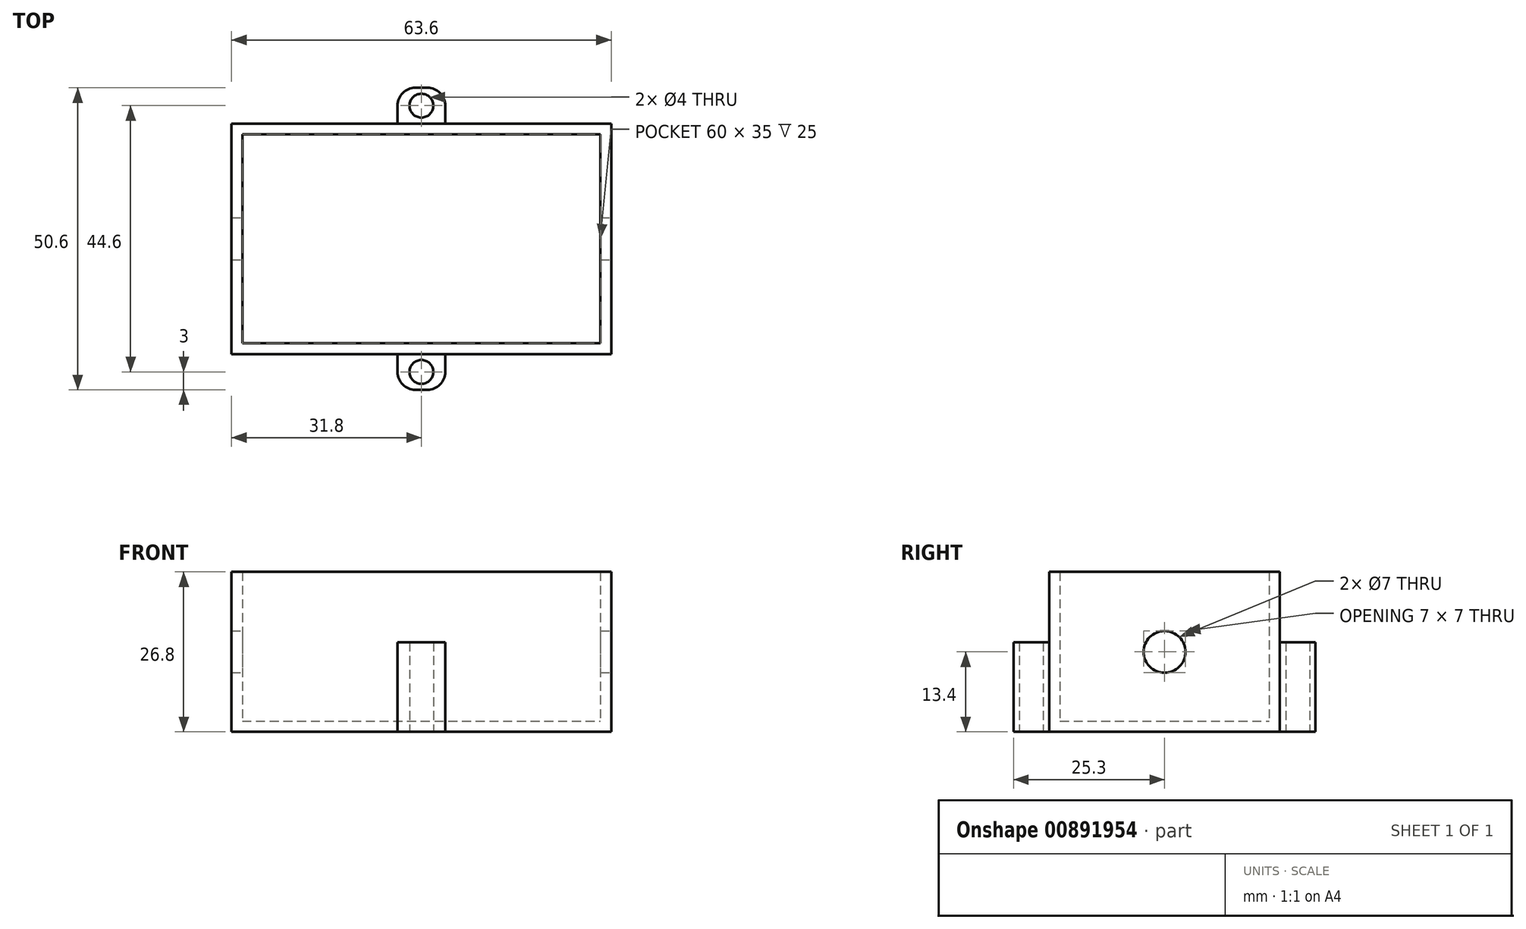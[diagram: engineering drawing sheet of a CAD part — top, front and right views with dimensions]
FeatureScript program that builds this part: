
annotation { "Feature Type Name" : "Feature", "Feature Type Description" : "" }
export const myFeature = defineFeature(function(context is Context, id is Id, definition is map)
    precondition{}
    {
        {
            var Q0;
            Q0=qCreatedBy(makeId("Top.planeOp"),FACE);
            var sketch = newSketch(context, id + "F0", { "sketchPlane" : qUnion([Q0])});
            skLineSegment(sketch, "E0.bottom", {"start": v(0, 0) * mm, "end": v(60, 0) * mm});
            skLineSegment(sketch, "E0.top", {"start": v(0, 35) * mm, "end": v(60, 35) * mm});
            skLineSegment(sketch, "E0.left", {"start": v(0, 0) * mm, "end": v(0, 35) * mm});
            skLineSegment(sketch, "E0.right", {"start": v(60, 0) * mm, "end": v(60, 35) * mm});
            skLineSegment(sketch, "E1.bottom", {"start": v(-1.8, 36.8) * mm, "end": v(61.8, 36.8) * mm});
            skLineSegment(sketch, "E1.top", {"start": v(-1.8, -1.8) * mm, "end": v(61.8, -1.8) * mm});
            skLineSegment(sketch, "E1.left", {"start": v(-1.8, 36.8) * mm, "end": v(-1.8, -1.8) * mm});
            skLineSegment(sketch, "E1.right", {"start": v(61.8, 36.8) * mm, "end": v(61.8, -1.8) * mm});
            skLineSegment(sketch, "E2", {"start": v(30, -1.8) * mm, "end": v(30, 36.8) * mm, "construction": true});
            skLineSegment(sketch, "E3", {"start": v(26, -1.8) * mm, "end": v(34, -1.8) * mm});
            skLineSegment(sketch, "E4", {"start": v(26, -1.8) * mm, "end": v(26, -4.8) * mm});
            skLineSegment(sketch, "E5", {"start": v(29, -7.8) * mm, "end": v(31, -7.8) * mm});
            skLineSegment(sketch, "E6", {"start": v(34, -4.8) * mm, "end": v(34, -1.8) * mm});
            skPoint(sketch, "E7.visualSharp", {"position": v(26, -7.8) * mm});
            skArc(sketch, "E7.filletArc", {"start": v(26, -4.8) * mm, "mid": v(26.88, -6.92) * mm, "end": v(29, -7.8) * mm});
            skPoint(sketch, "E8.visualSharp", {"position": v(34, -7.8) * mm});
            skArc(sketch, "E8.filletArc", {"start": v(31, -7.8) * mm, "mid": v(33.12, -6.92) * mm, "end": v(34, -4.8) * mm});
            skCircle(sketch, "E9", {"center": v(30, -4.8) * mm, "radius": 2 * mm});
            skLineSegment(sketch, "E10", {"start": v(0, 17.5) * mm, "end": v(60, 17.5) * mm, "construction": true});
            skLineSegment(sketch, "E11.MirrorCS", {"start": v(29, 42.8) * mm, "end": v(31, 42.8) * mm});
            skArc(sketch, "E12.MirrorCS", {"start": v(26, 39.8) * mm, "mid": v(26.88, 41.92) * mm, "end": v(29, 42.8) * mm});
            skLineSegment(sketch, "E13.MirrorCS", {"start": v(26, 36.8) * mm, "end": v(26, 39.8) * mm});
            skLineSegment(sketch, "E14.MirrorCS", {"start": v(34, 39.8) * mm, "end": v(34, 36.8) * mm});
            skArc(sketch, "E15.MirrorCS", {"start": v(31, 42.8) * mm, "mid": v(33.12, 41.92) * mm, "end": v(34, 39.8) * mm});
            skCircle(sketch, "E16.MirrorC", {"center": v(30, 39.8) * mm, "radius": 2 * mm});
            skSolve(sketch);
        }
        {
            var Q0;
            Q0=makeQuery(id+"F0.imprint","IMPRINT",FACE,{"disambiguationData":[TD([[makeQuery(id+"F0.imprint","IMPRINT",EDGE,{"derivedFrom":sQuery(id+"F0.wireOp",EDGE,"E0.bottom")}),-1.0]])]});
            var Q1;
            Q1=makeQuery(id+"F0.imprint","IMPRINT",FACE,{"disambiguationData":[TD([[makeQuery(id+"F0.imprint","IMPRINT",EDGE,{"derivedFrom":sQuery(id+"F0.wireOp",EDGE,"E0.bottom")}),1.0]])]});
            extrude(context, id + "F1", {"entities" : qUnion([Q0, Q1]), "depth" : 1.8 * mm, "offsetDistance" : 25 * mm});
        }
        {
            var Q0;
            Q0=makeQuery(id+"F1.opExtrude","CAP_FACE",FACE,{"disambiguationData":[OSD([sQuery(id+"F0.wireOp",EDGE,"E1.bottom"),sQuery(id+"F0.wireOp",EDGE,"E1.top"),sQuery(id+"F0.wireOp",EDGE,"E1.left"),sQuery(id+"F0.wireOp",EDGE,"E1.right")])],"isStart":false});
            var sketch = newSketch(context, id + "F2", { "sketchPlane" : qUnion([Q0])});
            skLineSegment(sketch, "E17.0", {"start": v(0, 0) * mm, "end": v(60, 0) * mm});
            skLineSegment(sketch, "E17.1", {"start": v(0, 35) * mm, "end": v(60, 35) * mm});
            skLineSegment(sketch, "E17.2", {"start": v(0, 0) * mm, "end": v(0, 35) * mm});
            skLineSegment(sketch, "E17.3", {"start": v(60, 0) * mm, "end": v(60, 35) * mm});
            skLineSegment(sketch, "E17.4", {"start": v(-1.8, 36.8) * mm, "end": v(61.8, 36.8) * mm});
            skLineSegment(sketch, "E17.5", {"start": v(-1.8, -1.8) * mm, "end": v(61.8, -1.8) * mm});
            skLineSegment(sketch, "E17.6", {"start": v(-1.8, 36.8) * mm, "end": v(-1.8, -1.8) * mm});
            skLineSegment(sketch, "E17.7", {"start": v(61.8, 36.8) * mm, "end": v(61.8, -1.8) * mm});
            skLineSegment(sketch, "E18", {"start": v(20.13, 4) * mm, "end": v(15.43, -1.8) * mm});
            skSolve(sketch);
        }
        {
            var Q0;
            Q0=makeQuery(id+"F2.imprint","IMPRINT",FACE,{"disambiguationData":[TD([[makeQuery(id+"F2.imprint","IMPRINT",EDGE,{"derivedFrom":sQuery(id+"F2.wireOp",EDGE,"E17.1")}),1.0]])]});
            extrude(context, id + "F3", {"entities" : qUnion([Q0]), "operationType" : NewBodyOperationType.ADD, "depth" : 25 * mm, "offsetDistance" : 25 * mm});
        }
        {
            var Q0;
            {var subQ0=sQuery(id+"F0.wireOp",EDGE,"E4");Q0=makeQuery(id+"F0.imprint","IMPRINT",FACE,{"disambiguationData":[TD([[makeQuery(id+"F0.imprint","IMPRINT",EDGE,{"derivedFrom":subQ0}),1.0]])]});}
            var Q1;
            Q1=makeQuery(id+"F0.imprint","IMPRINT",FACE,{"disambiguationData":[TD([[makeQuery(id+"F0.imprint","IMPRINT",EDGE,{"derivedFrom":sQuery(id+"F0.wireOp",EDGE,"E11.MirrorCS")}),-1.0]])]});
            extrude(context, id + "F4", {"entities" : qUnion([Q0, Q1]), "operationType" : NewBodyOperationType.ADD, "depth" : 15 * mm, "offsetDistance" : 25 * mm});
        }
        {
            var Q0;
            Q0=makeQuery(id+"F3.boolean.opBoolean","MERGE",FACE,{"derivedFrom":[makeQuery(id+"F1.opExtrude","SWEPT_FACE",FACE,{"disambiguationData":[OSD([sQuery(id+"F0.wireOp",EDGE,"E1.right")])]}),makeQuery(id+"F3.opExtrude","SWEPT_FACE",FACE,{"disambiguationData":[OSD([sQuery(id+"F2.wireOp",EDGE,"E17.7")])]})]});
            var sketch = newSketch(context, id + "F5", { "sketchPlane" : qUnion([Q0])});
            skCircle(sketch, "E19", {"center": v(17.5, 13.4) * mm, "radius": 3.5 * mm});
            skPoint(sketch, "E19.centerSnap0", {"position": v(17.5, 26.8) * mm});
            skPoint(sketch, "E19.centerSnap1", {"position": v(36.8, 13.4) * mm});
            skSolve(sketch);
        }
        {
            var Q0;
            Q0=makeQuery(id+"F5.imprint","IMPRINT",FACE,{"disambiguationData":[TD([[makeQuery(id+"F5.imprint","IMPRINT",EDGE,{"derivedFrom":sQuery(id+"F5.wireOp",EDGE,"E19")}),1.0]])]});
            extrude(context, id + "F6", {"entities" : qUnion([Q0]), "operationType" : NewBodyOperationType.REMOVE, "endBound" : BoundingType.THROUGH_ALL, "oppositeDirection" : true, "depth" : 25 * mm, "offsetDistance" : 25 * mm});
        }
    });
